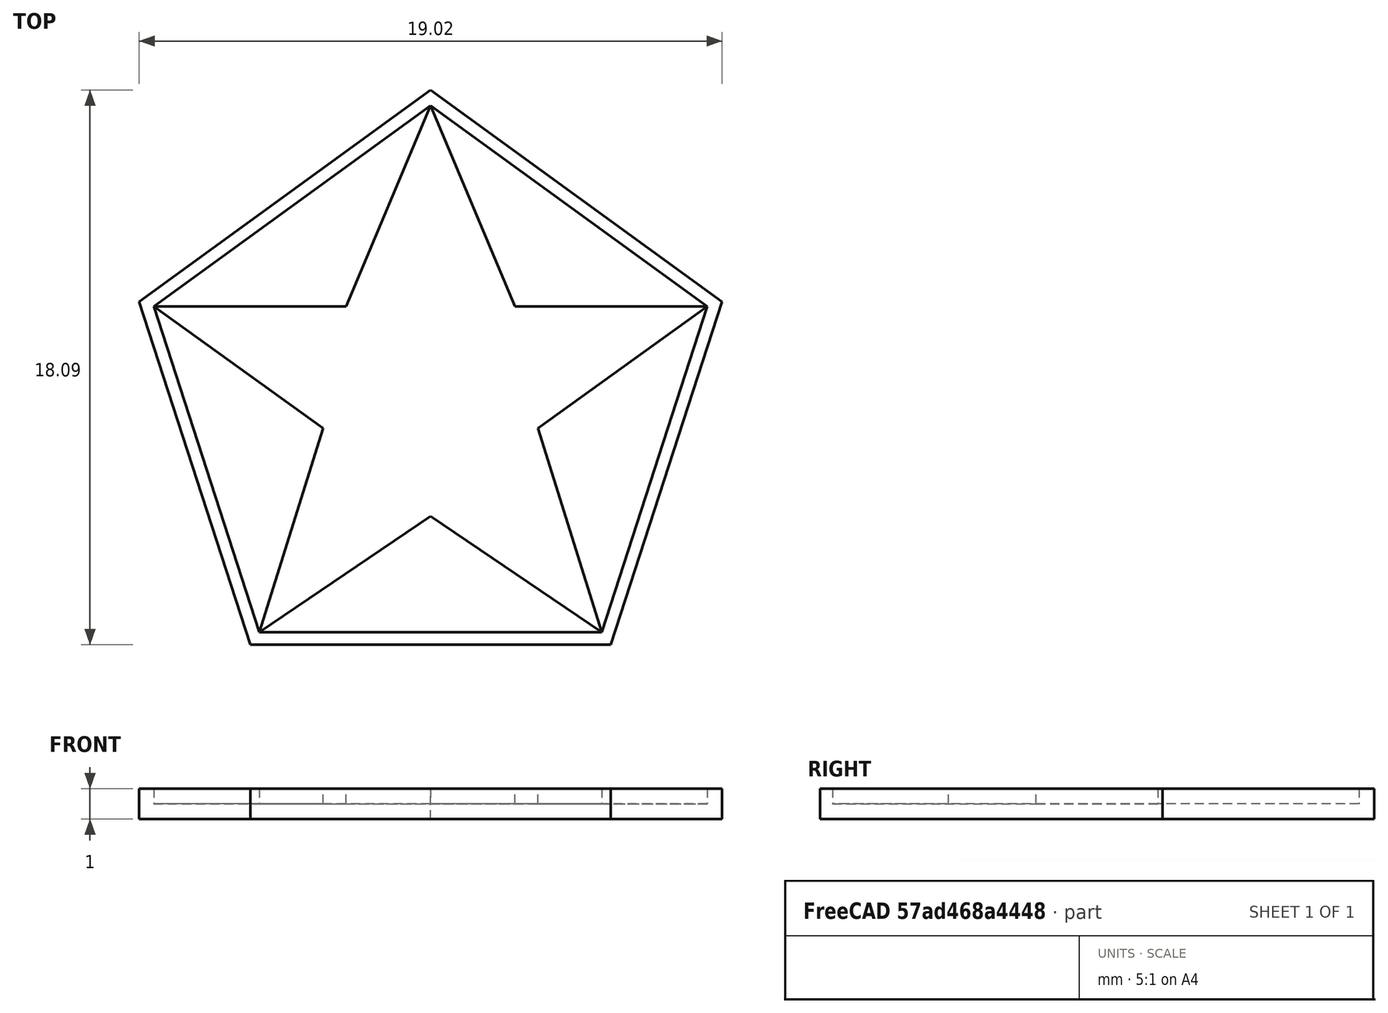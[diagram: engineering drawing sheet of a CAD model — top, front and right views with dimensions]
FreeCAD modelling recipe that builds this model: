
FCSTD DOCUMENT  (FreeCAD 1.0R39285 (Git))
Label: worksheet_exe.7
License: All rights reserved
LicenseURL: https://en.wikipedia.org/wiki/All_rights_reserved
objects: Sketcher::SketchObject×3, PartDesign::Pad×2, PartDesign::Pocket×1, PartDesign::Body×1
note: 16 computed .brp shape members not serialized (recipe doc carries the construction recipe); baked Part::Feature solids carry a one-line shape summary decoded from their .brp

FEATURE [Sketcher::SketchObject] Sketch
  ArcFitTolerance = 1e-06
  AttachmentSupport = -> [XY_Plane]
  FullyConstrained = true
  MakeInternals = false
  MapMode = 5
  sketch-geometry (7):
    g0: Circle [constr] CenterX=0 CenterY=0 CenterZ=0 NormalX=0 NormalY=0 NormalZ=1 AngleXU=0 Radius=10
    g1: GeomPoint X=0 Y=10 Z=0
    g2: LineSegment StartX=0 StartY=10 StartZ=0 EndX=-9.51057 EndY=3.09017 EndZ=0
    g3: LineSegment StartX=-9.51057 StartY=3.09017 StartZ=0 EndX=-5.87785 EndY=-8.09017 EndZ=0
    g4: LineSegment StartX=-5.87785 StartY=-8.09017 StartZ=0 EndX=5.87785 EndY=-8.09017 EndZ=0
    g5: LineSegment StartX=5.87785 StartY=-8.09017 StartZ=0 EndX=9.51057 EndY=3.09017 EndZ=0
    g6: LineSegment StartX=9.51057 StartY=3.09017 StartZ=0 EndX=0 EndY=10 EndZ=0
  constraints (18):
    c: Diameter(g0) = 20
    c: Coincident(g0,g-1)
    c: PointOnObject(g1,g0)
    c: Vertical(g1,g0)
    c: Coincident(g2,g1)
    c: PointOnObject(g2,g0)
    c: Coincident(g2,g3)
    c: PointOnObject(g3,g0)
    c: Coincident(g3,g4)
    c: PointOnObject(g4,g0)
    c: Coincident(g4,g5)
    c: PointOnObject(g5,g0)
    c: Coincident(g5,g6)
    c: Coincident(g6,g2)
    c: Equal(g2,g3)
    c: Equal(g4,g5)
    c: Equal(g6,g5)
    c: Equal(g4,g3)
FEATURE [PartDesign::Pad] Pad
  Direction = (0,0,1)
  Length = 1
  Length2 = 10
  Profile = -> Sketch
  ReferenceAxis = -> Sketch [N_Axis]
  Refine = true
  Suppressed = false
  Type = 0
FEATURE [Sketcher::SketchObject] Sketch001
  ArcFitTolerance = 1e-06
  AttachmentSupport = -> [Pad]
  FullyConstrained = true
  MakeInternals = false
  MapMode = 5
  Placement = pos=(0,0,1) rot=(0,0,1;0rad)
  sketch-geometry (6):
    g0: Circle [constr] CenterX=0 CenterY=0 CenterZ=0 NormalX=0 NormalY=0 NormalZ=1 AngleXU=0 Radius=9.5
    g1: LineSegment StartX=-2.41639e-11 StartY=9.5 StartZ=0 EndX=-9.03504 EndY=2.93566 EndZ=0
    g2: LineSegment StartX=-9.03504 StartY=2.93566 StartZ=0 EndX=-5.58396 EndY=-7.68566 EndZ=0
    g3: LineSegment StartX=-5.58396 StartY=-7.68566 StartZ=0 EndX=5.58396 EndY=-7.68566 EndZ=0
    g4: LineSegment StartX=5.58396 StartY=-7.68566 StartZ=0 EndX=9.03504 EndY=2.93566 EndZ=0
    g5: LineSegment StartX=9.03504 StartY=2.93566 StartZ=0 EndX=-2.41638e-11 EndY=9.5 EndZ=0
  constraints (17):
    c: Diameter(g0) = 19
    c: Coincident(g0,g-1)
    c: PointOnObject(g1,g0)
    c: PointOnObject(g1,g0)
    c: Coincident(g1,g2)
    c: PointOnObject(g2,g0)
    c: Coincident(g2,g3)
    c: PointOnObject(g3,g0)
    c: Horizontal(g3)
    c: Coincident(g3,g4)
    c: PointOnObject(g4,g0)
    c: Coincident(g4,g5)
    c: Coincident(g5,g1)
    c: Equal(g1,g2)
    c: Equal(g2,g3)
    c: Equal(g3,g4)
    c: Equal(g4,g5)
FEATURE [PartDesign::Pocket] Pocket
  BaseFeature = -> Pad
  Direction = (0,0,-1)
  Length = 0.5
  Length2 = 5
  Profile = -> Sketch001
  ReferenceAxis = -> Sketch001 [N_Axis]
  Refine = true
  Suppressed = false
  Type = 0
FEATURE [Sketcher::SketchObject] Sketch002
  ArcFitTolerance = 1e-06
  AttachmentSupport = -> [Pocket]
  ExternalGeometry = -> [Pocket]
  FullyConstrained = true
  MakeInternals = false
  MapMode = 5
  Placement = pos=(0,0,0.5) rot=(0,0,1;0rad)
  sketch-geometry (10):
    g0: LineSegment StartX=-9.03504 StartY=2.93566 StartZ=0 EndX=-2.75 EndY=2.93566 EndZ=0
    g1: LineSegment StartX=-2.75 StartY=2.93566 StartZ=0 EndX=-2.41638e-11 EndY=9.5 EndZ=0
    g2: LineSegment StartX=-2.41638e-11 StartY=9.5 StartZ=0 EndX=2.75 EndY=2.93566 EndZ=0
    g3: LineSegment StartX=2.75 StartY=2.93566 StartZ=0 EndX=9.03504 EndY=2.93566 EndZ=0
    g4: LineSegment StartX=9.03504 StartY=2.93566 StartZ=0 EndX=3.5 EndY=-1.03562 EndZ=0
    g5: LineSegment StartX=3.5 StartY=-1.03562 StartZ=0 EndX=5.58396 EndY=-7.68566 EndZ=0
    g6: LineSegment StartX=5.58396 StartY=-7.68566 StartZ=0 EndX=0 EndY=-3.9 EndZ=0
    g7: LineSegment StartX=0 StartY=-3.9 StartZ=0 EndX=-5.58396 EndY=-7.68566 EndZ=0
    g8: LineSegment StartX=-5.58396 StartY=-7.68566 StartZ=0 EndX=-3.5 EndY=-1.03562 EndZ=0
    g9: LineSegment StartX=-3.5 StartY=-1.03562 StartZ=0 EndX=-9.03504 EndY=2.93566 EndZ=0
  constraints (25):
    c: Coincident(g0,g-3)
    c: Coincident(g0,g1)
    c: Coincident(g1,g-4)
    c: Coincident(g1,g2)
    c: Coincident(g2,g3)
    c: Coincident(g3,g-5)
    c: Horizontal(g3)
    c: Coincident(g3,g4)
    c: Coincident(g4,g5)
    c: Coincident(g5,g-6)
    c: Coincident(g5,g6)
    c: PointOnObject(g6,g-2)
    c: Coincident(g6,g7)
    c: Coincident(g7,g-7)
    c: Coincident(g7,g8)
    c: Coincident(g8,g9)
    c: Coincident(g9,g0)
    c: Horizontal(g0)
    c: Equal(g1,g2)
    c: Equal(g9,g4)
    c: Equal(g8,g5)
    c: DistanceY(g6,g-1) = 3.9
    c: DistanceX(g8,g4) = 7
    c: DistanceX(g0,g2) = 5.5
    c: Distance(g4,g-1) = 3.65
FEATURE [PartDesign::Pad] Pad001
  BaseFeature = -> Pocket
  Direction = (0,0,1)
  Length = 0.5
  Length2 = 10
  Profile = -> Sketch002
  ReferenceAxis = -> Sketch002 [N_Axis]
  Refine = true
  Suppressed = false
  Type = 0
FEATURE [PartDesign::Body] Body
  AllowCompound = false
  Group = -> [Sketch,Pad,Sketch001,Pocket,Sketch002,Pad001]
  Origin = -> Origin
  Tip = -> Pad001
